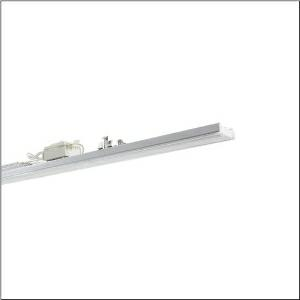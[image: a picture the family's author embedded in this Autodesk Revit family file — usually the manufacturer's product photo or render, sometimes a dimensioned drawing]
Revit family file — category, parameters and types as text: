
# Revit family: licross_r__11_recessed_mo_51tl11dn4axg_5468
name_source: partatom
category: Lighting Fixtures
units: mm (PartAtom-declared; Revit-internal decimal feet)

## family parameters
Cut with Voids When Loaded = No
Host = Face
Light Source = No
Part Type = Normal
Room Calculation Point = No
Round Connector Dimension = Use Diameter
Shared = No

## types (1)
- --- (1 x LED, 10080 lm, 56.7 W, 4000K)
    Apparent Load = 57 VA
    CIE Flux Codes = 89 96 99 100 100
    Color Rendering = 80
    Color Temperature = 4000K
    Default Elevation = 1800 mm
    Description = Licross® 11 Recessed MO, luminaire insert, of sheet steel, coil coated, white, length: 1.500mm, width: 66mm, height: 67mm, LED rated luminous flux: 10.080lm, light colour: 840, control gear: DALI 2, with plug, 5-pole, with phase selection, mains connection: 220..240V, AC, 50/60Hz, rated input power: 57W, internal wiring halogen-free, primary light control with lens, of plastic, primary optical cover: cover, of PMMA, light emission: direct distribution, primary light characteristic: symmetric, protection rating (complete): IP40, insulation class (complete): insulation class I (protective earthing), certification: CE, ENEC, VDE, UKCA, protection symbol: D if used in an environment without relevant dust loads with corresponding accessories, impact resistance: IK06, permissible ambient temperature for indoor applications: -25..+35°C, corresponds to IFS (International Featured Standards) requirements for safety and quality in the food industry, reducing of maximum allowable ambient temperature of 5°C with ceiling mounting, LABS conformity tested according to VDMA 24364:2018-05, packaging unit: 1 piece
    Height = 58 mm
    Lamp = 1 x LED
    Lamp Light Flux = 10080 lm
    Lamp Power = 56.7 W
    Lamp count = 1
    Length = 1500 mm
    Luminous efficacy = 178 lm/W
    Manufacturer = Siteco
    ModVariant = No
    Model = 51TL11DN4AXG
    Mounting Place = Ceiling
    Mounting Type = Pendant
    Number of Poles = 1
    OnlyDefault = Yes
    Power Factor = 1
    Product Name = Licross® 11 Recessed MO
    Product group = luminaire insert | ceiling pendant
    ProductGroupID = 902
    Protection Class = Protection class I
    Protection Degree = IP 40
    RLX_Detail_Level = 1
    RLX_Emergency_Light_Flux = 0 lm
    RLX_Emergency_Type = 0
    RLX_Emergency_Type_DB = No
    RlxData = <blob elided: 24413 chars, md5=8036b55e>
    Socket = socket
    Standby Power = 0 W
    System Light Flux = 10080 lm
    System Power = 57 W
    Type Comments = factory setting: luminous flux: 100 % | dim-lin: 254 | 378 mA
    Type Image = l_1296930.jpg
    URL = http://relux.com
    VarID = @adj_120129
    Voltage = 0 V
    Weight = 0.00 kg
    Width = 66 mm

## geometry (parser evidence)
native form markers: Blend x4, Sweep x12
no freeform markers — native parametric forms only
